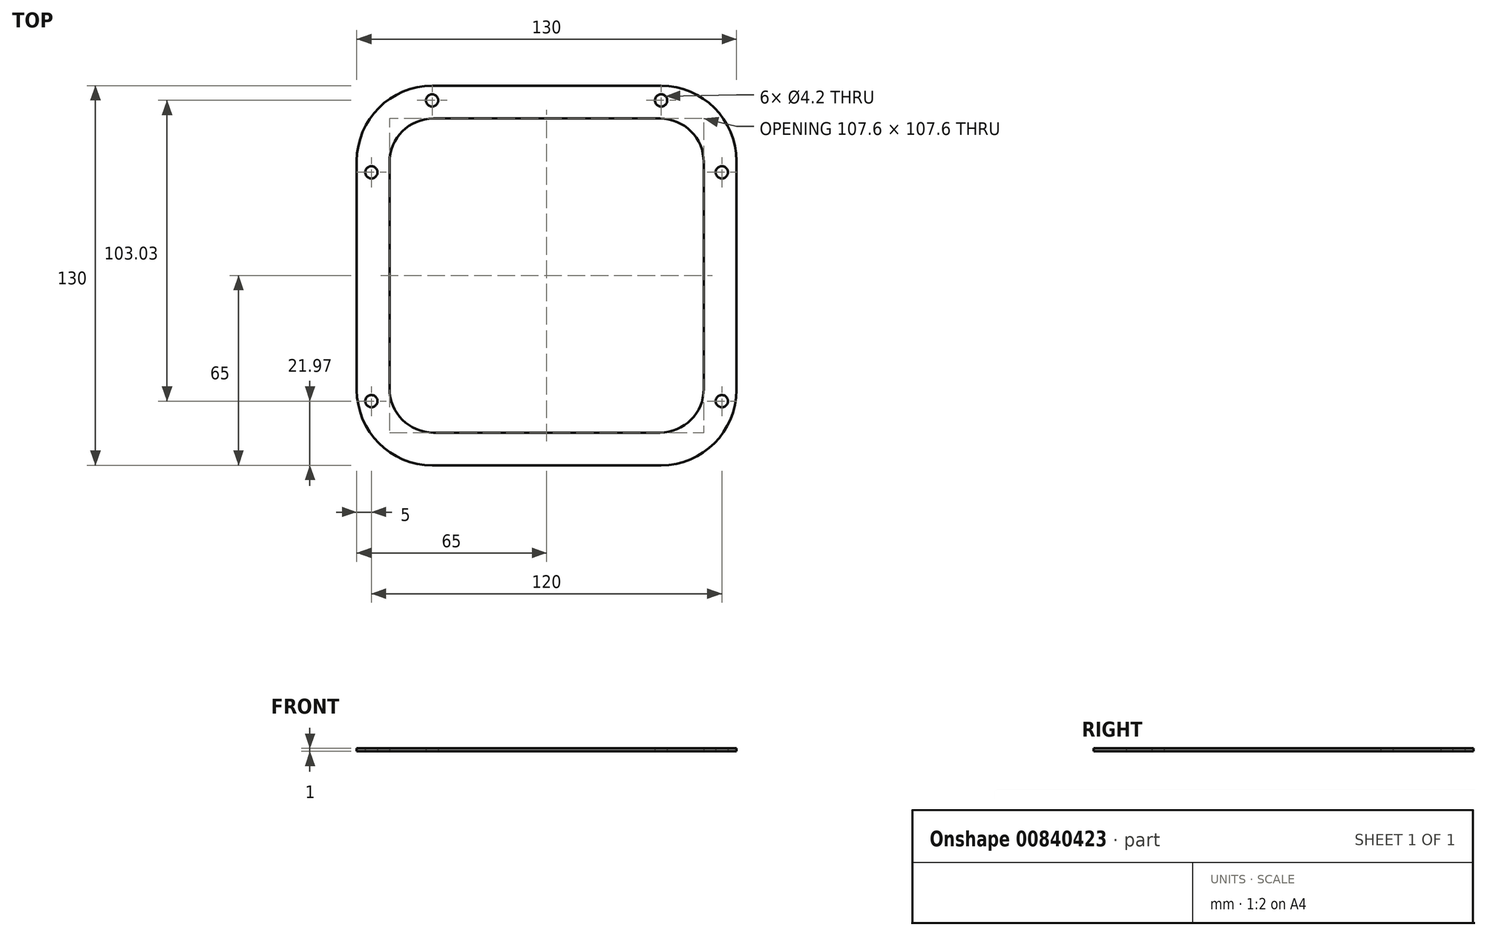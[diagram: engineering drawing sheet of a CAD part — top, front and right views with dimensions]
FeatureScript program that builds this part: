
annotation { "Feature Type Name" : "Feature", "Feature Type Description" : "" }
export const myFeature = defineFeature(function(context is Context, id is Id, definition is map)
    precondition{}
    {
        {
            var Q0;
            Q0=qCreatedBy(makeId("Top.planeOp"),FACE);
            var sketch = newSketch(context, id + "F0", { "sketchPlane" : qUnion([Q0])});
            skLineSegment(sketch, "E0.bottom", {"start": v(-39.2, 55) * mm, "end": v(39.2, 55) * mm});
            skLineSegment(sketch, "E0.top", {"start": v(-39.2, -55) * mm, "end": v(39.2, -55) * mm});
            skLineSegment(sketch, "E0.left", {"start": v(-55, 39.2) * mm, "end": v(-55, -39.2) * mm});
            skLineSegment(sketch, "E0.right", {"start": v(55, 39.2) * mm, "end": v(55, -39.2) * mm});
            skPoint(sketch, "E0.middle", {"position": v(0, 0) * mm});
            skLineSegment(sketch, "E1.bottom", {"start": v(39.2, 65) * mm, "end": v(-39.2, 65) * mm});
            skLineSegment(sketch, "E1.top", {"start": v(39.2, -65) * mm, "end": v(-39.2, -65) * mm});
            skLineSegment(sketch, "E1.left", {"start": v(65, 39.2) * mm, "end": v(65, -39.2) * mm});
            skLineSegment(sketch, "E1.right", {"start": v(-65, 39.2) * mm, "end": v(-65, -39.2) * mm});
            skLineSegment(sketch, "E2.0", {"start": v(-38.8, 53.8) * mm, "end": v(38.8, 53.8) * mm});
            skLineSegment(sketch, "E2.1", {"start": v(-53.8, 38.8) * mm, "end": v(-53.8, -38.8) * mm});
            skLineSegment(sketch, "E2.2", {"start": v(-38.8, -53.8) * mm, "end": v(38.8, -53.8) * mm});
            skLineSegment(sketch, "E2.3", {"start": v(53.8, 38.8) * mm, "end": v(53.8, -38.8) * mm});
            skPoint(sketch, "E3.visualSharp", {"position": v(-53.8, -53.8) * mm});
            skArc(sketch, "E3.filletArc", {"start": v(-53.8, -38.8) * mm, "mid": v(-49.4, -49.4) * mm, "end": v(-38.8, -53.8) * mm});
            skPoint(sketch, "E4.visualSharp", {"position": v(-55, -55) * mm});
            skArc(sketch, "E4.filletArc", {"start": v(-55, -39.2) * mm, "mid": v(-50.37, -50.37) * mm, "end": v(-39.2, -55) * mm});
            skPoint(sketch, "E5.visualSharp", {"position": v(53.8, -53.8) * mm});
            skArc(sketch, "E5.filletArc", {"start": v(38.8, -53.8) * mm, "mid": v(49.4, -49.4) * mm, "end": v(53.8, -38.8) * mm});
            skPoint(sketch, "E6.visualSharp", {"position": v(53.8, 53.8) * mm});
            skArc(sketch, "E6.filletArc", {"start": v(53.8, 38.8) * mm, "mid": v(49.4, 49.4) * mm, "end": v(38.8, 53.8) * mm});
            skPoint(sketch, "E7.visualSharp", {"position": v(-53.8, 53.8) * mm});
            skArc(sketch, "E7.filletArc", {"start": v(-38.8, 53.8) * mm, "mid": v(-49.4, 49.4) * mm, "end": v(-53.8, 38.8) * mm});
            skPoint(sketch, "E8.visualSharp", {"position": v(-55, 55) * mm});
            skArc(sketch, "E8.filletArc", {"start": v(-39.2, 55) * mm, "mid": v(-50.37, 50.37) * mm, "end": v(-55, 39.2) * mm});
            skPoint(sketch, "E9.visualSharp", {"position": v(55, 55) * mm});
            skArc(sketch, "E9.filletArc", {"start": v(55, 39.2) * mm, "mid": v(50.37, 50.37) * mm, "end": v(39.2, 55) * mm});
            skPoint(sketch, "E10.visualSharp", {"position": v(55, -55) * mm});
            skArc(sketch, "E10.filletArc", {"start": v(39.2, -55) * mm, "mid": v(50.37, -50.37) * mm, "end": v(55, -39.2) * mm});
            skPoint(sketch, "E11.visualSharp", {"position": v(65, -65) * mm});
            skArc(sketch, "E11.filletArc", {"start": v(39.2, -65) * mm, "mid": v(57.44, -57.44) * mm, "end": v(65, -39.2) * mm});
            skPoint(sketch, "E12.visualSharp", {"position": v(-65, -65) * mm});
            skArc(sketch, "E12.filletArc", {"start": v(-65, -39.2) * mm, "mid": v(-57.44, -57.44) * mm, "end": v(-39.2, -65) * mm});
            skPoint(sketch, "E13.visualSharp", {"position": v(65, 65) * mm});
            skArc(sketch, "E13.filletArc", {"start": v(65, 39.2) * mm, "mid": v(57.44, 57.44) * mm, "end": v(39.2, 65) * mm});
            skPoint(sketch, "E14.visualSharp", {"position": v(-65, 65) * mm});
            skArc(sketch, "E14.filletArc", {"start": v(-39.2, 65) * mm, "mid": v(-57.44, 57.44) * mm, "end": v(-65, 39.2) * mm});
            skLineSegment(sketch, "E15.0", {"start": v(60, 35.37) * mm, "end": v(60, -43.03) * mm});
            skLineSegment(sketch, "E16.0", {"start": v(-60, 35.37) * mm, "end": v(-60, -43.03) * mm});
            skCircle(sketch, "E17", {"center": v(60, 35.37) * mm, "radius": 2.1 * mm});
            skCircle(sketch, "E18", {"center": v(60, -43.03) * mm, "radius": 2.1 * mm});
            skCircle(sketch, "E19", {"center": v(-60, 35.37) * mm, "radius": 2.1 * mm});
            skCircle(sketch, "E20", {"center": v(-60, -43.03) * mm, "radius": 2.1 * mm});
            skLineSegment(sketch, "E21.0", {"start": v(39.2, 60) * mm, "end": v(-39.2, 60) * mm});
            skCircle(sketch, "E22", {"center": v(-39.2, 60) * mm, "radius": 2.1 * mm});
            skCircle(sketch, "E23", {"center": v(39.2, 60) * mm, "radius": 2.1 * mm});
            skSolve(sketch);
        }
        {
            var Q0;
            Q0 = qSketchRegion(id + "F0", true);
            var Q1;
            Q1=makeQuery(id+"F0.imprint","IMPRINT",FACE,{"disambiguationData":[TD([[makeQuery(id+"F0.imprint","IMPRINT",EDGE,{"derivedFrom":sQuery(id+"F0.wireOp",EDGE,"E0.bottom")}),-1.0]])]});
            extrude(context, id + "F1", {"entities" : qUnion([Q0, Q1]), "depth" : 1 * mm, "offsetDistance" : 25 * mm});
        }
    });
